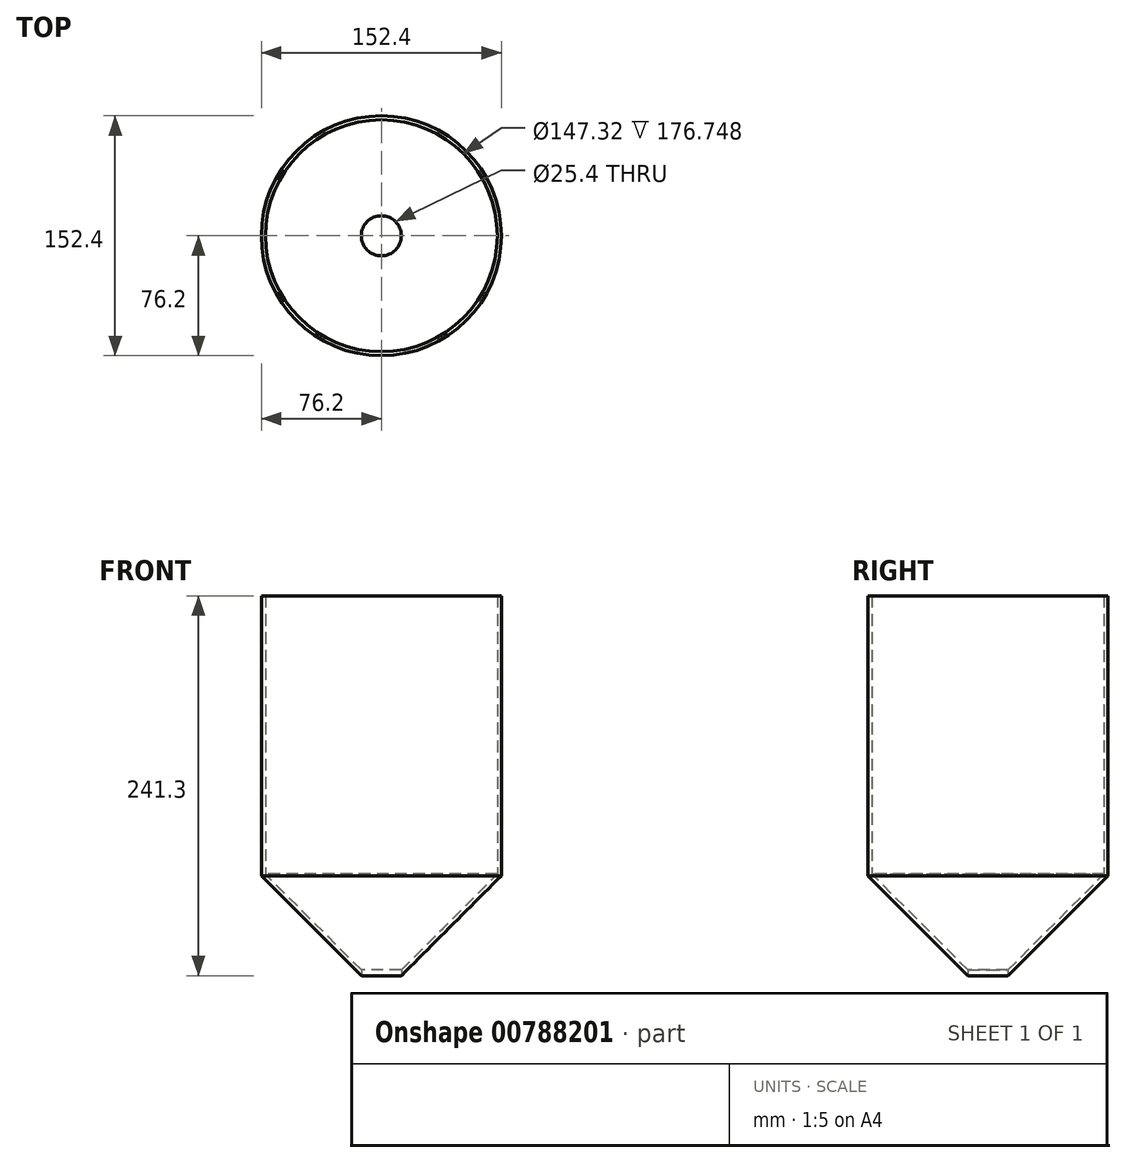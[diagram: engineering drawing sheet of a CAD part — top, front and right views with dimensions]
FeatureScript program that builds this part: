
annotation { "Feature Type Name" : "Feature", "Feature Type Description" : "" }
export const myFeature = defineFeature(function(context is Context, id is Id, definition is map)
    precondition{}
    {
        {
            var Q0;
            Q0=qCreatedBy(makeId("Top.planeOp"),FACE);
            var sketch = newSketch(context, id + "F0", { "sketchPlane" : qUnion([Q0])});
            skCircle(sketch, "E0", {"center": v(0, 0) * mm, "radius": 76.2 * mm});
            skSolve(sketch);
        }
        {
            var Q0;
            Q0=makeQuery(id+"F0.imprint","IMPRINT",FACE,{"disambiguationData":[TD([[makeQuery(id+"F0.imprint","IMPRINT",EDGE,{"derivedFrom":sQuery(id+"F0.wireOp",EDGE,"E0")}),1.0]])]});
            extrude(context, id + "F1", {"entities" : qUnion([Q0]), "depth" : 254 * mm, "offsetDistance" : 25.4 * mm});
        }
        {
            var Q0;
            Q0=makeQuery(id+"F1.opExtrude","CAP_EDGE",EDGE,{"disambiguationData":[OSD([sQuery(id+"F0.wireOp",EDGE,"E0")])],"isStart":true});
            chamfer(context, id + "F2", {"entities" : qUnion([Q0]), "width" : 76.2 * mm, "tangentPropagation" : true});
        }
        {
            var Q0;
            Q0=qCreatedBy(makeId("Top.planeOp"),FACE);
            var sketch = newSketch(context, id + "F3", { "sketchPlane" : qUnion([Q0])});
            skCircle(sketch, "E1", {"center": v(0, 0) * mm, "radius": 12.7 * mm});
            skSolve(sketch);
        }
        {
            var Q0;
            Q0=makeQuery(id+"F1.opExtrude","CAP_FACE",FACE,{"disambiguationData":[OSD([sQuery(id+"F0.wireOp",EDGE,"E0")])],"isStart":false});
            shell(context, id + "F4", {"entities" : qUnion([Q0]), "thickness" : 2.54 * mm});
        }
        {
            var Q0;
            Q0=sQuery(id+"F3.wireOp",VERTEX,"E1.center");
            var Q1;
            Q1=makeQuery(id+"F1.opExtrude","SWEPT_BODY",BODY,{"disambiguationData":[OSD([sQuery(id+"F0.wireOp",EDGE,"E0")])]});
            hole(context, id + "F5", {"style" : HoleStyle.SIMPLE, "endStyle" : HoleEndStyle.THROUGH, "oppositeDirection" : true, "holeDiameter" : 25.4 * mm, "majorDiameter" : 6.35 * mm, "isTappedThrough" : true, "tappedDepth" : 12.7 * mm, "tapClearance" : 3, "locations" : qUnion([Q0]), "scope" : qUnion([Q1])});
        }
    });
